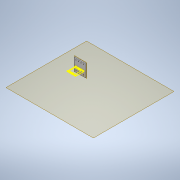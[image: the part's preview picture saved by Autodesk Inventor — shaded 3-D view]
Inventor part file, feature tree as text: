
AUTODESK INVENTOR PART (.ipt)
format: ipt  version: 2022 (Build 260153000, 153)  size: 210,944 bytes
history: native  units: mm
features: reference x9, other x6, extrude x4, sketch x4, plane x3, fillet x1, projected_geometry x1
ambient origin geometry x8: Origin, YZ Plane, XZ Plane, XY Plane, X Axis, Y Axis, Z Axis, Center Point
bodies: Solid1 (feature_tree)
feature tree (28):
  plane  "Work Plane1"
  extrude  "Extrusion1"  Depth=3.0mm
  plane  "Work Plane2"
  plane  "Work Plane3"
  extrude  "Extrusion2"  Depth=15.573864mm
  extrude  "Extrusion3"  Depth=3.0mm
  extrude  "Extrusion4"  Depth=3.0mm TaperAngle=0.0deg
  fillet  "Fillet1"  Radius=3.0mm
  sketch  "Sketch1"  dims[d0=3.0mm d1=0.0mm d2=0.2mm d3=3.0mm]
  reference  "Reference1"
  reference  "Reference2"
  sketch  "Sketch2"  dims[d4=0.3mm d5=15.573864mm]
  reference  "Reference3"
  reference  "Reference4"
  reference  "Reference5"
  reference  "Reference6"
  reference  "Reference7"
  reference  "Reference8"
  reference  "Reference9"
  sketch  "Sketch3"  dims[d6=14.523864mm d7=3.0mm]
  sketch  "Sketch4"  dims[d8=10.0mm d9=0.0mm d10=3.0mm d11=0.0mm d12=3.0mm d13=0.0mm d14=4.0mm d15=10.0mm]
  projected_geometry  "Projected Loop1"
  other  "Solids Feeder Head Assembly.iam"
  other  "body:1"
  other  "<userpath>\OneDrive - Imperial College London\ROBOICP\Final Assembly\Final Assembly.iam"
  other  "Final Assembly.iam"
  other  "Reaction Printer:1"
  other  "Print_Head_v5:1"
